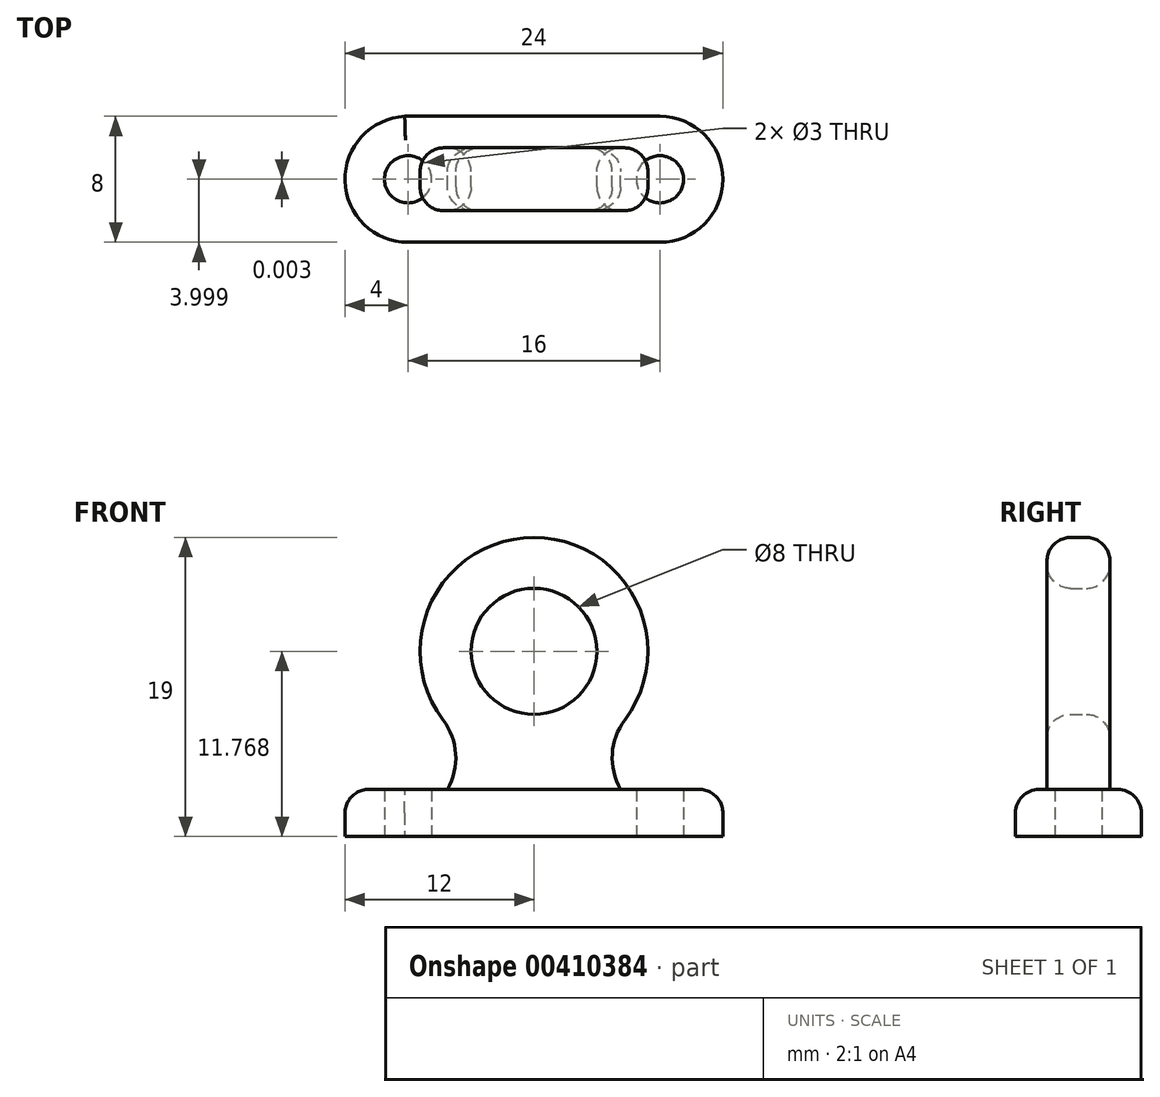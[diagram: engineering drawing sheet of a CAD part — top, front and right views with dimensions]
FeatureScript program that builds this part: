
annotation { "Feature Type Name" : "Feature", "Feature Type Description" : "" }
export const myFeature = defineFeature(function(context is Context, id is Id, definition is map)
    precondition{}
    {
        {
            var Q0;
            Q0=qCreatedBy(makeId("Top.planeOp"),FACE);
            var sketch = newSketch(context, id + "F0", { "sketchPlane" : qUnion([Q0])});
            skLineSegment(sketch, "E0", {"start": v(-8.21, 4) * mm, "end": v(8, 4) * mm});
            skArc(sketch, "E1", {"start": v(8, -4) * mm, "mid": v(12, 0) * mm, "end": v(8, 4) * mm});
            skLineSegment(sketch, "E2", {"start": v(8, -4) * mm, "end": v(-8, -4) * mm});
            skArc(sketch, "E3", {"start": v(-8.21, 4) * mm, "mid": v(-12, -0.1) * mm, "end": v(-8, -4) * mm});
            skLineSegment(sketch, "E4", {"start": v(-8, 0) * mm, "end": v(8, 0) * mm, "construction": true});
            skCircle(sketch, "E5", {"center": v(-8, 0) * mm, "radius": 1.5 * mm});
            skCircle(sketch, "E6", {"center": v(8, 0) * mm, "radius": 1.5 * mm});
            skSolve(sketch);
        }
        {
            var Q0;
            Q0=makeQuery(id+"F0.imprint","IMPRINT",FACE,{"disambiguationData":[TD([[makeQuery(id+"F0.imprint","IMPRINT",EDGE,{"derivedFrom":sQuery(id+"F0.wireOp",EDGE,"E0")}),-1.0]])]});
            extrude(context, id + "F1", {"entities" : qUnion([Q0]), "depth" : 3 * mm, "offsetDistance" : 25 * mm});
        }
        {
            var Q0;
            Q0=qCreatedBy(makeId("Front.planeOp"),FACE);
            var sketch = newSketch(context, id + "F2", { "sketchPlane" : qUnion([Q0])});
            skLineSegment(sketch, "E7.0", {"start": v(8, 3) * mm, "end": v(-8, 3) * mm});
            skArc(sketch, "E8", {"start": v(5.77, 7.41) * mm, "mid": v(0, 19) * mm, "end": v(-5.77, 7.41) * mm});
            skLineSegment(sketch, "E9", {"start": v(0, 3) * mm, "end": v(0, 11.77) * mm, "construction": true});
            skPoint(sketch, "E9.endSnap0", {"position": v(0, 3) * mm});
            skArc(sketch, "E10", {"start": v(-5.5, 3) * mm, "mid": v(-4.97, 5.25) * mm, "end": v(-5.77, 7.41) * mm});
            skArc(sketch, "E11", {"start": v(5.77, 7.41) * mm, "mid": v(4.97, 5.25) * mm, "end": v(5.5, 3) * mm});
            skCircle(sketch, "E12", {"center": v(0, 11.77) * mm, "radius": 4 * mm});
            skSolve(sketch);
        }
        {
            var Q0;
            {var subQ0=sQuery(id+"F2.wireOp",EDGE,"xTBZJoAd-OCCK-0P2C-9tp4-rfreanSKMqLF");Q0=makeQuery(id+"F2.imprint","IMPRINT",FACE,{"disambiguationData":[TD([[makeQuery(id+"F2.imprint","IMPRINT",EDGE,{"derivedFrom":subQ0}),-1.0]])]});}
            var Q1;
            Q1=makeQuery(id+"F2.imprint","IMPRINT",FACE,{"disambiguationData":[TD([[makeQuery(id+"F2.imprint","IMPRINT",EDGE,{"derivedFrom":sQuery(id+"F2.wireOp",EDGE,"E8")}),1.0]])]});
            extrude(context, id + "F3", {"entities" : qUnion([Q0, Q1]), "operationType" : NewBodyOperationType.ADD, "depth" : 4 * mm, "offsetDistance" : 25 * mm, "symmetric" : true});
        }
        {
            var Q0;
            Q0=makeQuery(id+"F3.opExtrude","CAP_EDGE",EDGE,{"disambiguationData":[OSD([sQuery(id+"F2.wireOp",EDGE,"E8")])],"isStart":false});
            var Q1;
            Q1=makeQuery(id+"F3.opExtrude","CAP_EDGE",EDGE,{"disambiguationData":[OSD([sQuery(id+"F2.wireOp",EDGE,"E8")])],"isStart":true});
            var Q2;
            Q2=makeQuery(id+"F1.opExtrude","CAP_EDGE",EDGE,{"disambiguationData":[OSD([sQuery(id+"F0.wireOp",EDGE,"E2")])],"isStart":false});
            var Q3;
            Q3=makeQuery(id+"F3.opExtrude","CAP_EDGE",EDGE,{"disambiguationData":[OSD([sQuery(id+"F2.wireOp",EDGE,"E12")])],"isStart":false});
            var Q4;
            Q4=makeQuery(id+"F3.opExtrude","CAP_EDGE",EDGE,{"disambiguationData":[OSD([sQuery(id+"F2.wireOp",EDGE,"E12")])],"isStart":true});
            fillet(context, id + "F4", {"entities" : qUnion([Q0, Q1, Q2, Q3, Q4]), "radius" : 1.5 * mm, "tangentPropagation" : true, "allowEdgeOverflow" : false});
        }
    });
